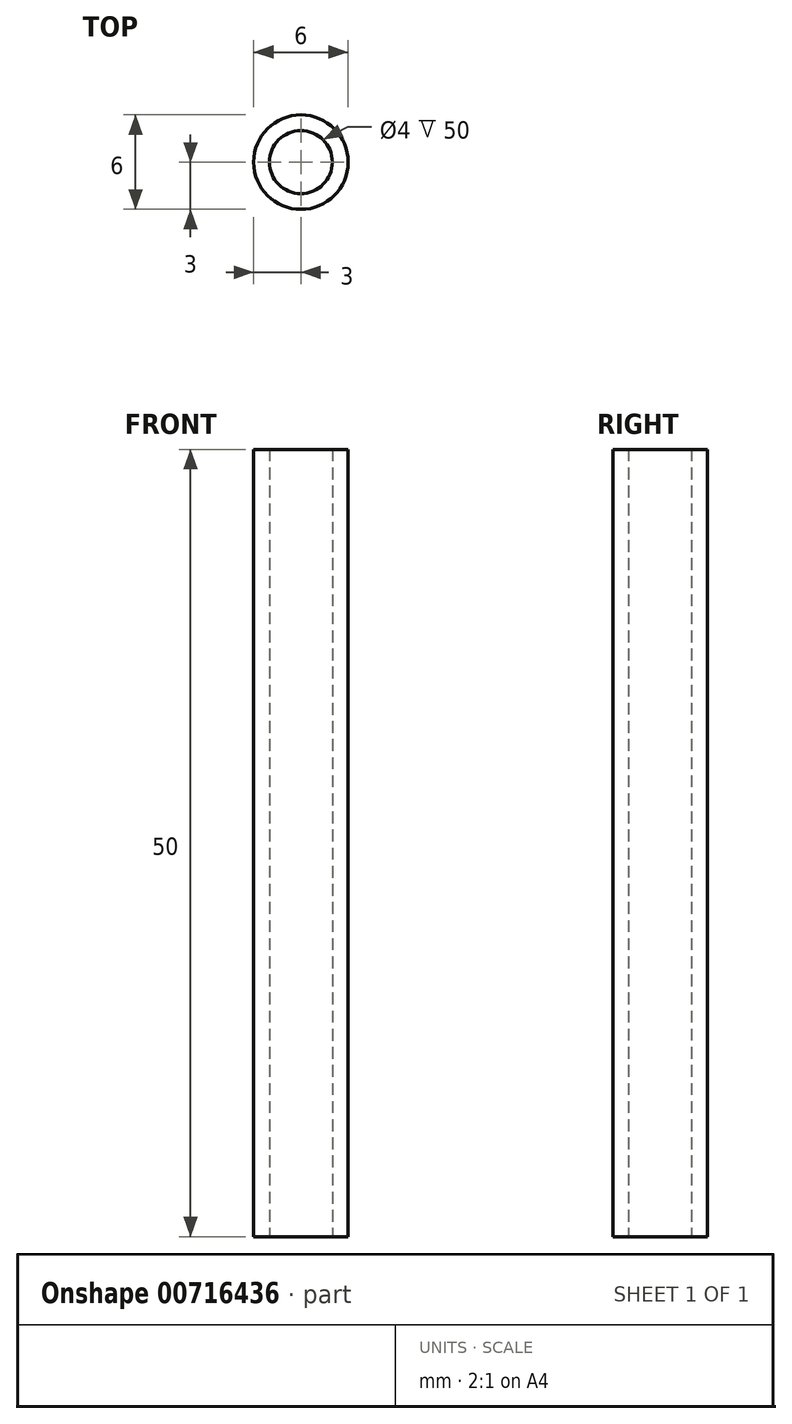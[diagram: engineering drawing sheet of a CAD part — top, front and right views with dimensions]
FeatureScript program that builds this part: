
annotation { "Feature Type Name" : "Feature", "Feature Type Description" : "" }
export const myFeature = defineFeature(function(context is Context, id is Id, definition is map)
    precondition{}
    {
        {
            var Q0;
            Q0=qCreatedBy(makeId("Top.planeOp"),FACE);
            var sketch = newSketch(context, id + "F0", { "sketchPlane" : qUnion([Q0])});
            skCircle(sketch, "E0", {"center": v(0, 0) * mm, "radius": 3 * mm});
            skCircle(sketch, "E1", {"center": v(0, 0) * mm, "radius": 2 * mm});
            skSolve(sketch);
        }
        {
            var Q0;
            Q0 = qSketchRegion(id + "F0", true);
            extrude(context, id + "F1", {"entities" : qUnion([Q0]), "depth" : 50 * mm, "offsetDistance" : 25 * mm});
        }
    });
